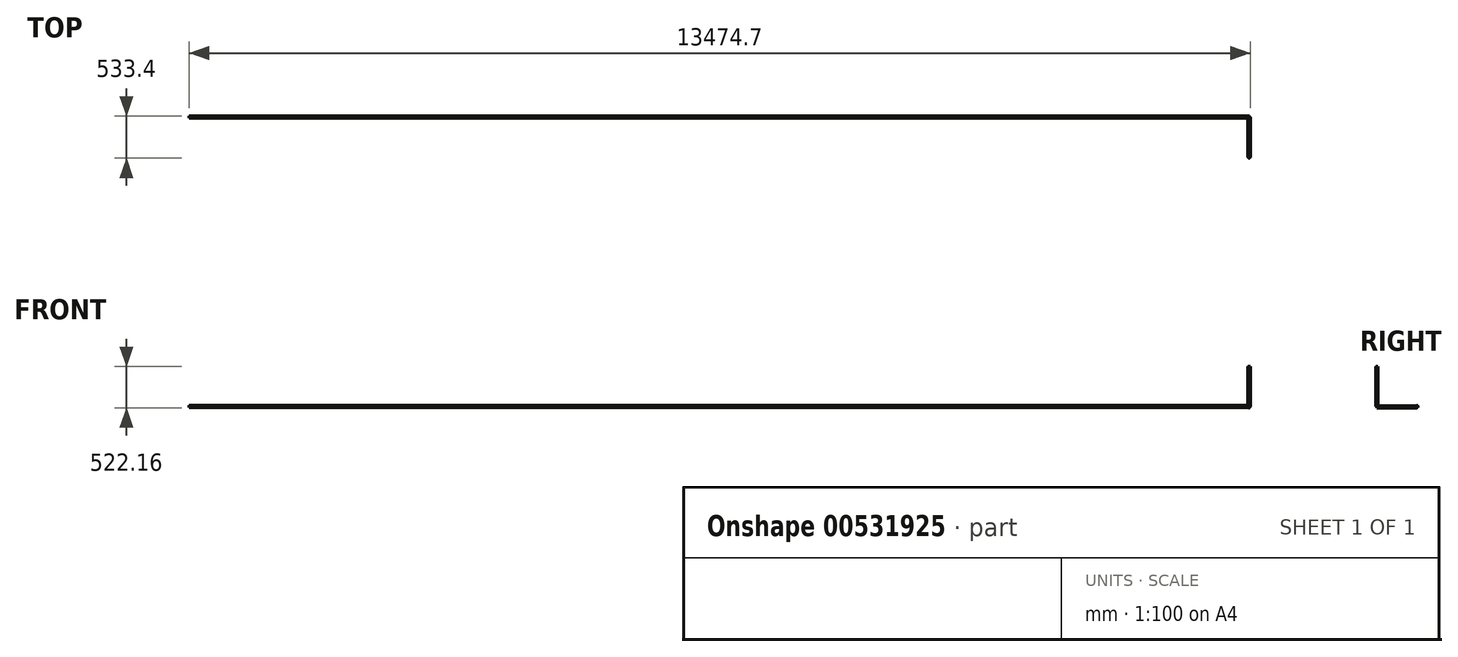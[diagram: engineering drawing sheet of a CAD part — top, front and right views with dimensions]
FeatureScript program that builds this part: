
annotation { "Feature Type Name" : "Feature", "Feature Type Description" : "" }
export const myFeature = defineFeature(function(context is Context, id is Id, definition is map)
    precondition{}
    {
        {
            var Q0;
            Q0=qCreatedBy(makeId("Right.planeOp"),FACE);
            var sketch = newSketch(context, id + "F0", { "sketchPlane" : qUnion([Q0])});
            skCircle(sketch, "E0", {"center": v(0, 0) * mm, "radius": 12.7 * mm});
            skSolve(sketch);
        }
        {
            var Q0;
            Q0=qSketchRegion(id+"F0",true);
            extrude(context, id + "F1", {"entities" : qUnion([Q0]), "oppositeDirection" : true, "depth" : 13462 * mm, "offsetDistance" : 25.4 * mm});
        }
        {
            var Q0;
            Q0=qCreatedBy(makeId("Front.planeOp"),FACE);
            var sketch = newSketch(context, id + "F2", { "sketchPlane" : qUnion([Q0])});
            skCircle(sketch, "E1", {"center": v(0, -1.46) * mm, "radius": 12.7 * mm});
            skSolve(sketch);
        }
        {
            var Q0;
            Q0=qSketchRegion(id+"F2",true);
            extrude(context, id + "F3", {"entities" : qUnion([Q0]), "operationType" : NewBodyOperationType.ADD, "depth" : 508 * mm, "offsetDistance" : 25.4 * mm});
        }
        {
            var Q0;
            Q0=makeQuery(id+"F3.opExtrude","CAP_FACE",FACE,{"disambiguationData":[OSD([sQuery(id+"F2.wireOp",EDGE,"E1")])],"isStart":false});
            var sketch = newSketch(context, id + "F4", { "sketchPlane" : qUnion([Q0])});
            skPoint(sketch, "E2", {"position": v(0, -1.46) * mm});
            skSolve(sketch);
        }
        {
            var Q0;
            Q0=qCreatedBy(makeId("Top.planeOp"),FACE);
            var sketch = newSketch(context, id + "F5", { "sketchPlane" : qUnion([Q0])});
            skCircle(sketch, "E3", {"center": v(0, -508) * mm, "radius": 12.7 * mm});
            skSolve(sketch);
        }
        {
            var Q0;
            Q0=makeQuery(id+"F5.imprint","IMPRINT",FACE,{"disambiguationData":[TD([[makeQuery(id+"F5.imprint","IMPRINT",EDGE,{"derivedFrom":sQuery(id+"F5.wireOp",EDGE,"E3")}),1.0]])]});
            extrude(context, id + "F6", {"entities" : qUnion([Q0]), "operationType" : NewBodyOperationType.ADD, "depth" : 508 * mm, "offsetDistance" : 25.4 * mm});
        }
    });
